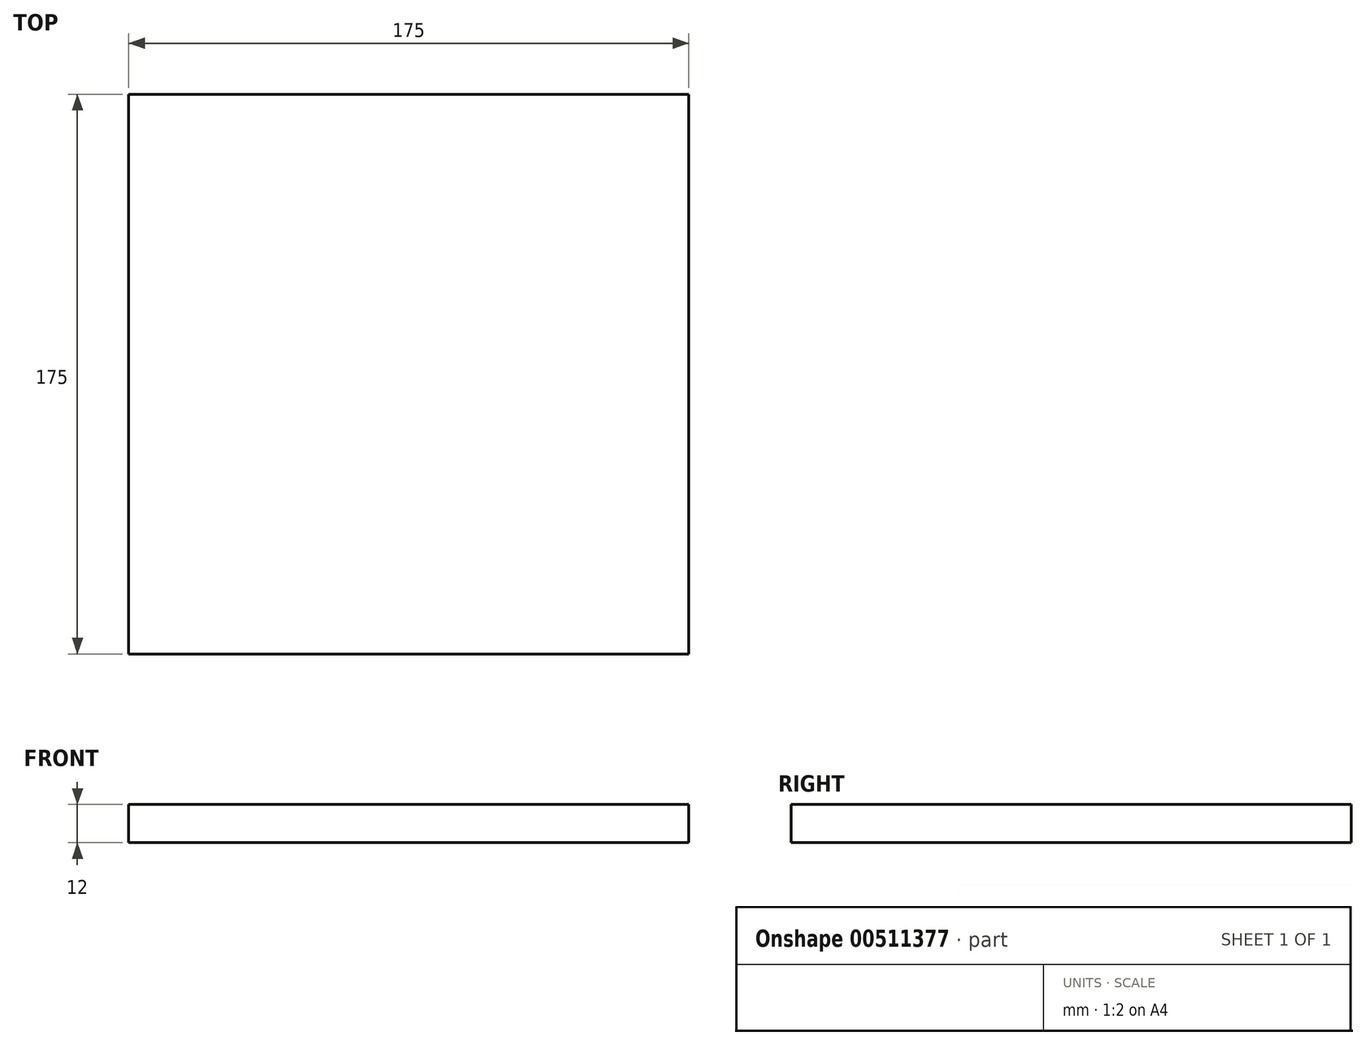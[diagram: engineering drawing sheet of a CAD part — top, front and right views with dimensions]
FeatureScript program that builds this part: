
annotation { "Feature Type Name" : "Feature", "Feature Type Description" : "" }
export const myFeature = defineFeature(function(context is Context, id is Id, definition is map)
    precondition{}
    {
        {
            var Q0;
            Q0=qCreatedBy(makeId("Front.planeOp"),FACE);
            var sketch = newSketch(context, id + "F0", { "sketchPlane" : qUnion([Q0])});
            skLineSegment(sketch, "E0.bottom", {"start": v(-87.5, -6) * mm, "end": v(87.5, -6) * mm});
            skLineSegment(sketch, "E0.top", {"start": v(-87.5, 6) * mm, "end": v(87.5, 6) * mm});
            skLineSegment(sketch, "E0.left", {"start": v(-87.5, -6) * mm, "end": v(-87.5, 6) * mm});
            skLineSegment(sketch, "E0.right", {"start": v(87.5, -6) * mm, "end": v(87.5, 6) * mm});
            skPoint(sketch, "E0.middle", {"position": v(0, 0) * mm});
            skSolve(sketch);
        }
        {
            var Q0;
            Q0=makeQuery(id+"F0.imprint","IMPRINT",FACE,{"disambiguationData":[TD([[makeQuery(id+"F0.imprint","IMPRINT",EDGE,{"derivedFrom":sQuery(id+"F0.wireOp",EDGE,"E0.bottom")}),1.0]])]});
            extrude(context, id + "F1", {"entities" : qUnion([Q0]), "endBound" : BoundingType.SYMMETRIC, "depth" : 175 * mm, "offsetDistance" : 25.4 * mm});
        }
        {
            var Q0;
            Q0=makeQuery(id+"F1.opExtrude","SWEPT_FACE",FACE,{"disambiguationData":[OSD([sQuery(id+"F0.wireOp",EDGE,"E0.top")])]});
            var sketch = newSketch(context, id + "F2", { "sketchPlane" : qUnion([Q0])});
            skLineSegment(sketch, "E1.bottom", {"start": v(25.02, -87.5) * mm, "end": v(-25.02, -87.5) * mm});
            skLineSegment(sketch, "E1.top", {"start": v(25.02, 87.5) * mm, "end": v(-25.02, 87.5) * mm});
            skLineSegment(sketch, "E1.left", {"start": v(25.02, -87.5) * mm, "end": v(25.02, 87.5) * mm});
            skLineSegment(sketch, "E1.right", {"start": v(-25.02, -87.5) * mm, "end": v(-25.02, 87.5) * mm});
            skPoint(sketch, "E1.middle", {"position": v(0, 0) * mm});
            skLineSegment(sketch, "E2.bottom", {"start": v(42.04, -87.5) * mm, "end": v(25.02, -87.5) * mm});
            skLineSegment(sketch, "E2.top", {"start": v(42.04, 87.5) * mm, "end": v(25.02, 87.5) * mm});
            skLineSegment(sketch, "E2.left", {"start": v(42.04, -87.5) * mm, "end": v(42.04, 87.5) * mm});
            skLineSegment(sketch, "E3.bottom", {"start": v(-25.02, -87.5) * mm, "end": v(-42.04, -87.5) * mm});
            skLineSegment(sketch, "E3.top", {"start": v(-25.02, 87.5) * mm, "end": v(-42.04, 87.5) * mm});
            skLineSegment(sketch, "E3.right", {"start": v(-42.04, -87.5) * mm, "end": v(-42.04, 87.5) * mm});
            skLineSegment(sketch, "E4.bottom", {"start": v(42.04, 2.42) * mm, "end": v(59.06, 2.42) * mm});
            skLineSegment(sketch, "E4.top", {"start": v(42.04, 52.45) * mm, "end": v(59.06, 52.45) * mm});
            skLineSegment(sketch, "E4.left", {"start": v(42.04, 2.42) * mm, "end": v(42.04, 52.45) * mm});
            skLineSegment(sketch, "E4.right", {"start": v(59.06, 2.42) * mm, "end": v(59.06, 52.45) * mm});
            skLineSegment(sketch, "E5.bottom", {"start": v(-42.04, 2.42) * mm, "end": v(-59.05, 2.42) * mm});
            skLineSegment(sketch, "E5.top", {"start": v(-42.04, 52.45) * mm, "end": v(-59.06, 52.45) * mm});
            skLineSegment(sketch, "E5.left", {"start": v(-42.04, 2.42) * mm, "end": v(-42.04, 52.45) * mm});
            skLineSegment(sketch, "E5.right", {"start": v(-59.05, 2.42) * mm, "end": v(-59.06, 52.45) * mm});
            skSolve(sketch);
        }
    });
